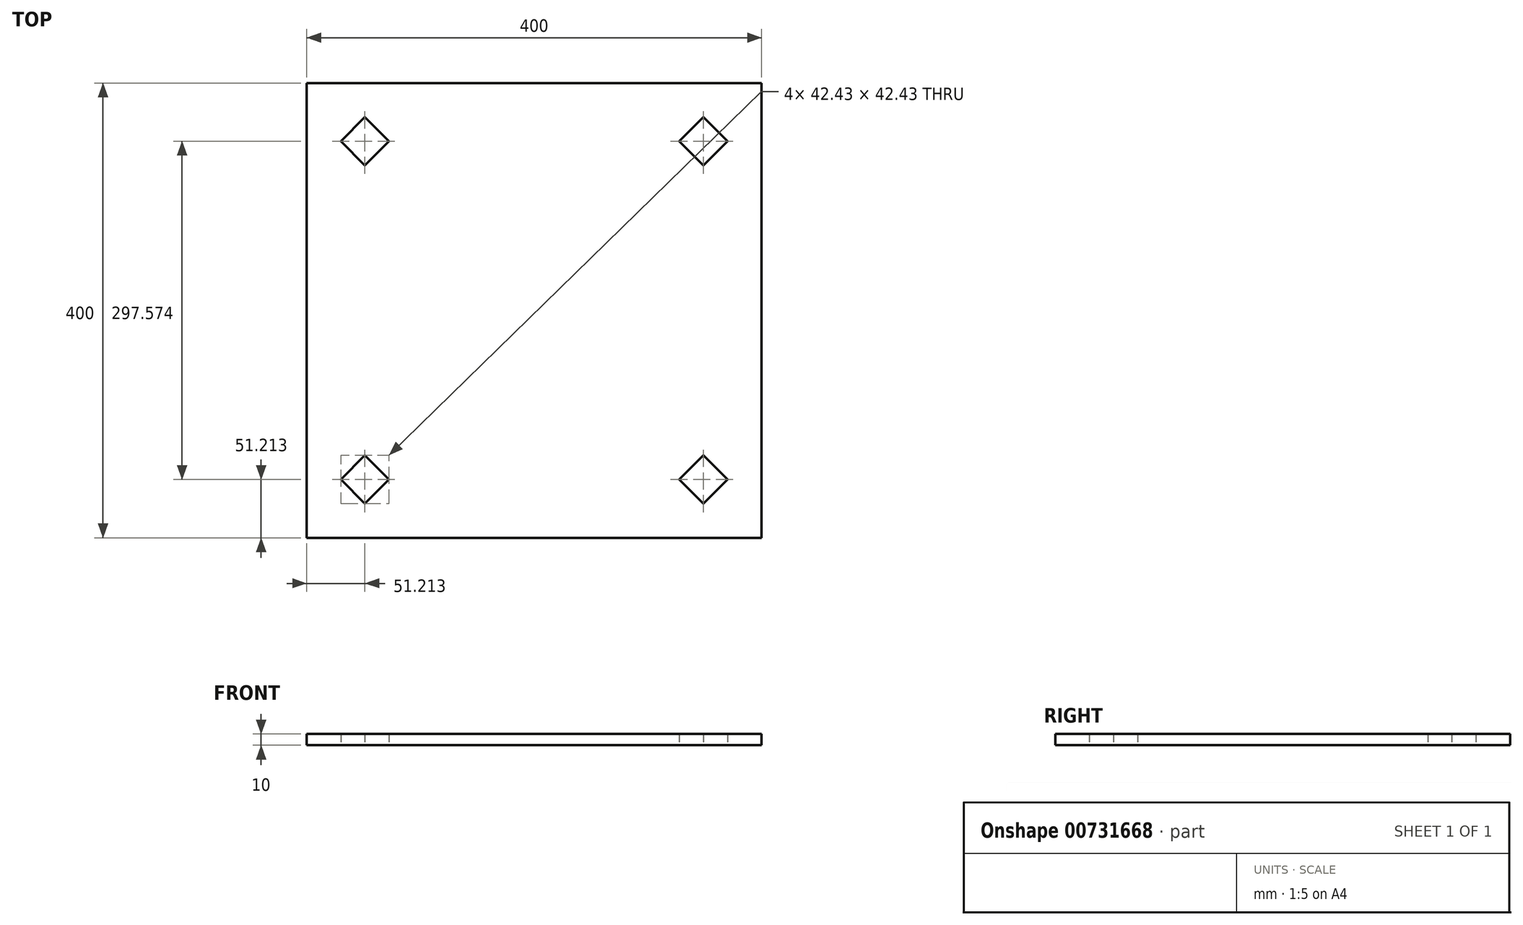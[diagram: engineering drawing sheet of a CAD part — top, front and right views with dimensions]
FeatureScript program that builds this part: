
annotation { "Feature Type Name" : "Feature", "Feature Type Description" : "" }
export const myFeature = defineFeature(function(context is Context, id is Id, definition is map)
    precondition{}
    {
        {
            var Q0;
            Q0=qCreatedBy(makeId("Top.planeOp"),FACE);
            var sketch = newSketch(context, id + "F0", { "sketchPlane" : qUnion([Q0])});
            skLineSegment(sketch, "E0.bottom", {"start": v(200, 200) * mm, "end": v(-200, 200) * mm});
            skLineSegment(sketch, "E0.top", {"start": v(200, -200) * mm, "end": v(-200, -200) * mm});
            skLineSegment(sketch, "E0.left", {"start": v(200, 200) * mm, "end": v(200, -200) * mm});
            skLineSegment(sketch, "E0.right", {"start": v(-200, 200) * mm, "end": v(-200, -200) * mm});
            skPoint(sketch, "E0.middle", {"position": v(0, 0) * mm});
            skLineSegment(sketch, "E1", {"start": v(-200, 200) * mm, "end": v(200, -200) * mm});
            skLineSegment(sketch, "E2", {"start": v(-148.79, -127.57) * mm, "end": v(-170, -148.79) * mm});
            skLineSegment(sketch, "E3", {"start": v(-170, -148.79) * mm, "end": v(-148.79, -170) * mm});
            skLineSegment(sketch, "E4", {"start": v(-148.79, -170) * mm, "end": v(-127.57, -148.79) * mm});
            skLineSegment(sketch, "E5", {"start": v(-127.57, -148.79) * mm, "end": v(-148.79, -127.57) * mm});
            skLineSegment(sketch, "E6", {"start": v(-200, 0) * mm, "end": v(200, 0) * mm});
            skLineSegment(sketch, "E7.MirrorCS", {"start": v(-127.57, 148.79) * mm, "end": v(-148.79, 127.57) * mm});
            skLineSegment(sketch, "E8.MirrorCS", {"start": v(-148.79, 127.57) * mm, "end": v(-170, 148.79) * mm});
            skLineSegment(sketch, "E9.MirrorCS", {"start": v(-170, 148.79) * mm, "end": v(-148.79, 170) * mm});
            skLineSegment(sketch, "E10.MirrorCS", {"start": v(-148.79, 170) * mm, "end": v(-127.57, 148.79) * mm});
            skLineSegment(sketch, "E11.MirrorCS", {"start": v(148.79, 127.57) * mm, "end": v(127.57, 148.79) * mm});
            skLineSegment(sketch, "E12.MirrorCS", {"start": v(127.57, 148.79) * mm, "end": v(148.79, 170) * mm});
            skLineSegment(sketch, "E13.MirrorCS", {"start": v(148.79, 170) * mm, "end": v(170, 148.79) * mm});
            skLineSegment(sketch, "E14.MirrorCS", {"start": v(170, 148.79) * mm, "end": v(148.79, 127.57) * mm});
            skLineSegment(sketch, "E15.MirrorCS", {"start": v(148.79, -127.57) * mm, "end": v(127.57, -148.79) * mm});
            skLineSegment(sketch, "E16.MirrorCS", {"start": v(127.57, -148.79) * mm, "end": v(148.79, -170) * mm});
            skLineSegment(sketch, "E17.MirrorCS", {"start": v(148.79, -170) * mm, "end": v(170, -148.79) * mm});
            skLineSegment(sketch, "E18.MirrorCS", {"start": v(170, -148.79) * mm, "end": v(148.79, -127.57) * mm});
            skLineSegment(sketch, "E19", {"start": v(159.4, 159.4) * mm, "end": v(200, 200) * mm});
            skSolve(sketch);
        }
        {
            var Q0;
            {var subQ1=sQuery(id+"F0.wireOp",EDGE,"E0.bottom");Q0=makeQuery(id+"F0.imprint","IMPRINT",FACE,{"disambiguationData":[TD([[makeQuery(id+"F0.imprint","IMPRINT",EDGE,{"derivedFrom":subQ1}),1.0]])]});}
            var Q1;
            {var subQ5=sQuery(id+"F0.wireOp",EDGE,"E8.MirrorCS");Q1=makeQuery(id+"F0.imprint","IMPRINT",FACE,{"disambiguationData":[TD([[makeQuery(id+"F0.imprint","IMPRINT",EDGE,{"derivedFrom":subQ5}),1.0]])]});}
            var Q2;
            {var subQ5=sQuery(id+"F0.wireOp",EDGE,"E0.top");Q2=makeQuery(id+"F0.imprint","IMPRINT",FACE,{"disambiguationData":[TD([[makeQuery(id+"F0.imprint","IMPRINT",EDGE,{"derivedFrom":subQ5}),-1.0]])]});}
            var Q3;
            {var subQ8=sQuery(id+"F0.wireOp",EDGE,"E18.MirrorCS");Q3=makeQuery(id+"F0.imprint","IMPRINT",FACE,{"disambiguationData":[TD([[makeQuery(id+"F0.imprint","IMPRINT",EDGE,{"derivedFrom":subQ8}),-1.0]])]});}
            extrude(context, id + "F1", {"entities" : qUnion([Q0, Q1, Q2, Q3]), "depth" : 10 * mm, "offsetDistance" : 25 * mm});
        }
    });
